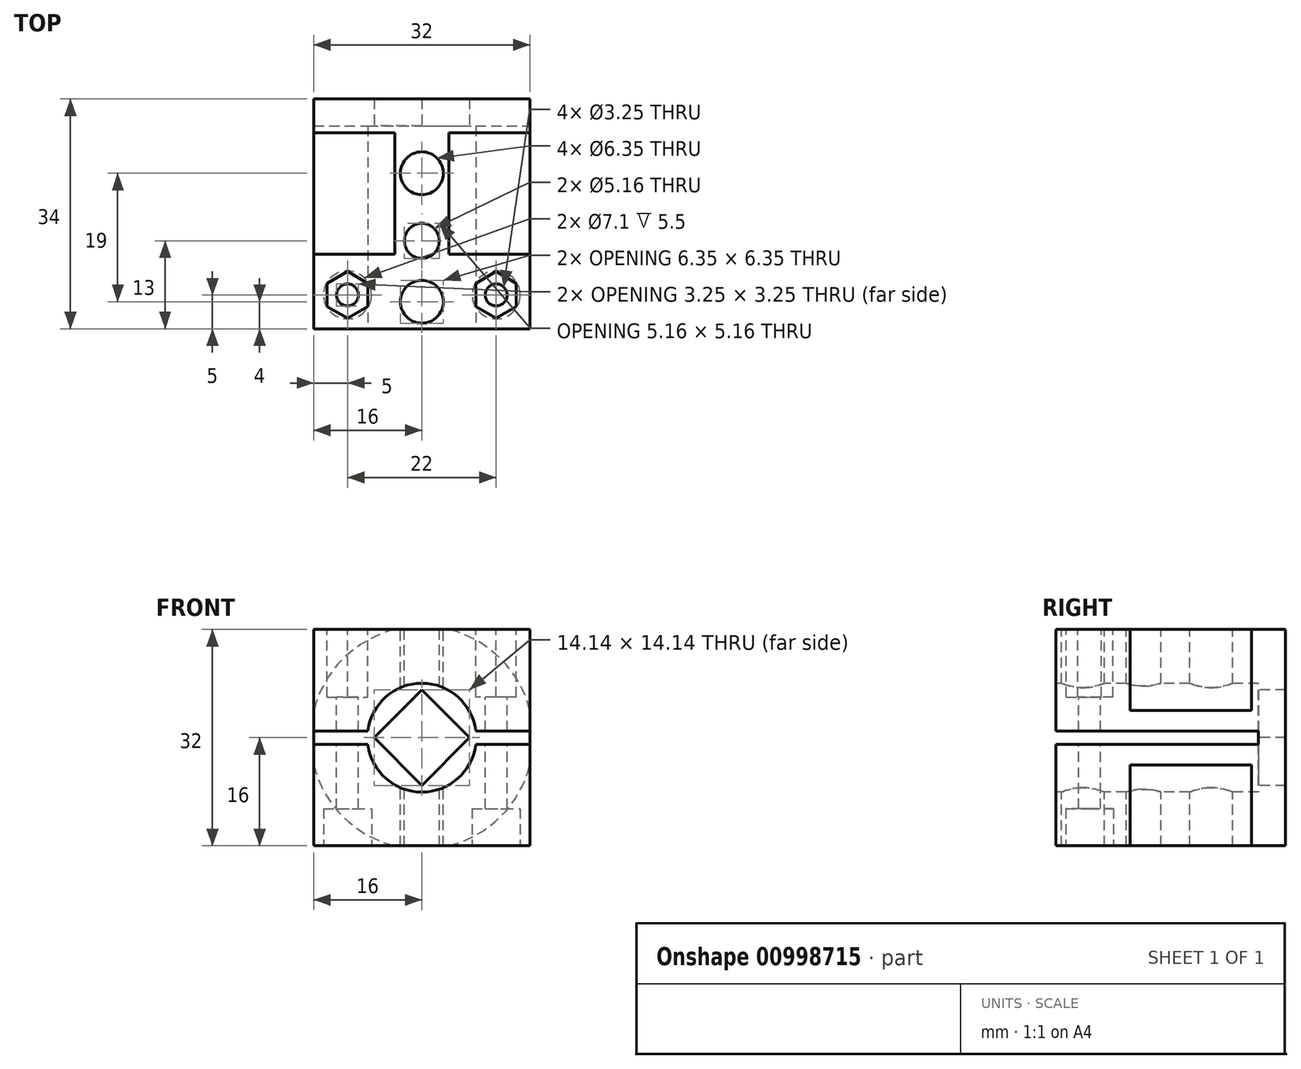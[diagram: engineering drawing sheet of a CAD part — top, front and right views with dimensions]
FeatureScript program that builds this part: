
annotation { "Feature Type Name" : "Feature", "Feature Type Description" : "" }
export const myFeature = defineFeature(function(context is Context, id is Id, definition is map)
    precondition{}
    {
        {
            var Q0;
            Q0=qCreatedBy(makeId("Front.planeOp"),FACE);
            var sketch = newSketch(context, id + "F0", { "sketchPlane" : qUnion([Q0])});
            skLineSegment(sketch, "E0.bottom", {"start": v(16, -16) * mm, "end": v(-16, -16) * mm});
            skLineSegment(sketch, "E0.top", {"start": v(16, 16) * mm, "end": v(-16, 16) * mm});
            skLineSegment(sketch, "E0.left", {"start": v(16, -16) * mm, "end": v(16, 16) * mm});
            skLineSegment(sketch, "E0.right", {"start": v(-16, -16) * mm, "end": v(-16, 16) * mm});
            skPoint(sketch, "E0.middle", {"position": v(0, 0) * mm});
            skSolve(sketch);
        }
        {
            var Q0;
            Q0 = qSketchRegion(id + "F0", true);
            extrude(context, id + "F1", {"entities" : qUnion([Q0]), "endBound" : BoundingType.SYMMETRIC, "depth" : 34 * mm, "offsetDistance" : 25 * mm});
        }
        {
            var Q0;
            Q0=qCreatedBy(makeId("Front.planeOp"),FACE);
            var sketch = newSketch(context, id + "F2", { "sketchPlane" : qUnion([Q0])});
            skCircle(sketch, "E1", {"center": v(0, 0) * mm, "radius": 8.05 * mm});
            skSolve(sketch);
        }
        {
            var Q0;
            Q0 = qSketchRegion(id + "F2", true);
            extrude(context, id + "F3", {"entities" : qUnion([Q0]), "operationType" : NewBodyOperationType.REMOVE, "oppositeDirection" : true, "depth" : 13 * mm, "offsetDistance" : 25 * mm, "hasSecondDirection" : true, "secondDirectionOppositeDirection" : false, "secondDirectionDepth" : 17 * mm});
        }
        {
            var Q0;
            Q0=qCreatedBy(makeId("Right.planeOp"),FACE);
            var sketch = newSketch(context, id + "F4", { "sketchPlane" : qUnion([Q0])});
            skLineSegment(sketch, "E2", {"start": v(-19, 1) * mm, "end": v(13, 1) * mm});
            skLineSegment(sketch, "E3", {"start": v(13, 1) * mm, "end": v(13, -1) * mm});
            skLineSegment(sketch, "E4", {"start": v(13, -1) * mm, "end": v(-19, -1) * mm});
            skLineSegment(sketch, "E5", {"start": v(-19, -1) * mm, "end": v(-19, 1) * mm});
            skSolve(sketch);
        }
        {
            var Q0;
            Q0=makeQuery(id+"F4.imprint","IMPRINT",FACE,{"disambiguationData":[TD([[makeQuery(id+"F4.imprint","IMPRINT",EDGE,{"derivedFrom":sQuery(id+"F4.wireOp",EDGE,"E2")}),-1.0]])]});
            extrude(context, id + "F5", {"entities" : qUnion([Q0]), "operationType" : NewBodyOperationType.REMOVE, "endBound" : BoundingType.THROUGH_ALL, "oppositeDirection" : true, "depth" : 25 * mm, "offsetDistance" : 25 * mm, "hasSecondDirection" : true, "secondDirectionBound" : SecondDirectionBoundingType.THROUGH_ALL, "secondDirectionOppositeDirection" : false, "secondDirectionDepth" : 25 * mm});
        }
        {
            var Q0;
            Q0=qCreatedBy(makeId("Top.planeOp"),FACE);
            var sketch = newSketch(context, id + "F6", { "sketchPlane" : qUnion([Q0])});
            skLineSegment(sketch, "E6", {"start": v(0, -53.15) * mm, "end": v(0, 37.76) * mm, "construction": true});
            skCircle(sketch, "E7", {"center": v(0, 6) * mm, "radius": 3.18 * mm});
            skCircle(sketch, "E8", {"center": v(0, -4) * mm, "radius": 2.58 * mm});
            skCircle(sketch, "E9", {"center": v(0, -13) * mm, "radius": 3.18 * mm});
            skLineSegment(sketch, "E10.0.0", {"start": v(7.99, 13) * mm, "end": v(-7.99, 13) * mm, "construction": true});
            skSolve(sketch);
        }
        {
            var Q0;
            Q0 = qSketchRegion(id + "F6", true);
            extrude(context, id + "F7", {"entities" : qUnion([Q0]), "operationType" : NewBodyOperationType.REMOVE, "endBound" : BoundingType.THROUGH_ALL, "oppositeDirection" : true, "depth" : 25 * mm, "offsetDistance" : 25 * mm, "hasSecondDirection" : true, "secondDirectionBound" : SecondDirectionBoundingType.THROUGH_ALL, "secondDirectionOppositeDirection" : false, "secondDirectionDepth" : 25 * mm});
        }
        {
            var Q0;
            Q0=makeQuery(id+"F1.opExtrude","SWEPT_FACE",FACE,{"disambiguationData":[OSD([sQuery(id+"F0.wireOp",EDGE,"E0.top")])]});
            var sketch = newSketch(context, id + "F8", { "sketchPlane" : qUnion([Q0])});
            skLineSegment(sketch, "E11.0", {"start": v(16, -17) * mm, "end": v(-16, -17) * mm, "construction": true});
            skLineSegment(sketch, "E12.1", {"start": v(16, -17) * mm, "end": v(16, 17) * mm, "construction": true});
            skLineSegment(sketch, "E13.0", {"start": v(16, 17) * mm, "end": v(-16, 17) * mm, "construction": true});
            skLineSegment(sketch, "E14.0", {"start": v(-16, -17) * mm, "end": v(-16, 17) * mm, "construction": true});
            skCircle(sketch, "E15", {"center": v(-11, -12) * mm, "radius": 1.63 * mm});
            skCircle(sketch, "E16", {"center": v(11, -12) * mm, "radius": 1.63 * mm});
            skSolve(sketch);
        }
        {
            var Q0;
            Q0 = qSketchRegion(id + "F8", true);
            extrude(context, id + "F9", {"entities" : qUnion([Q0]), "operationType" : NewBodyOperationType.REMOVE, "endBound" : BoundingType.THROUGH_ALL, "oppositeDirection" : true, "depth" : 25 * mm, "offsetDistance" : 25 * mm});
        }
        {
            var Q0;
            Q0=makeQuery(id+"F1.opExtrude","SWEPT_FACE",FACE,{"disambiguationData":[OSD([sQuery(id+"F0.wireOp",EDGE,"E0.bottom")])]});
            var sketch = newSketch(context, id + "F10", { "sketchPlane" : qUnion([Q0])});
            skCircle(sketch, "E17", {"center": v(11, 12) * mm, "radius": 3.55 * mm});
            skCircle(sketch, "E18", {"center": v(-11, 12) * mm, "radius": 3.55 * mm});
            skSolve(sketch);
        }
        {
            var Q0;
            Q0=makeQuery(id+"F1.opExtrude","SWEPT_FACE",FACE,{"disambiguationData":[OSD([sQuery(id+"F0.wireOp",EDGE,"E0.top")])]});
            var sketch = newSketch(context, id + "F11", { "sketchPlane" : qUnion([Q0])});
            skCircle(sketch, "E19.cCircle", {"center": v(-11, -12) * mm, "radius": 3 * mm, "construction": true});
            skLineSegment(sketch, "E19.0", {"start": v(-8, -10.27) * mm, "end": v(-8, -13.73) * mm});
            skLineSegment(sketch, "E19.1", {"start": v(-8, -13.73) * mm, "end": v(-11, -15.46) * mm});
            skLineSegment(sketch, "E19.2", {"start": v(-11, -15.46) * mm, "end": v(-14, -13.73) * mm});
            skLineSegment(sketch, "E19.3", {"start": v(-14, -13.73) * mm, "end": v(-14, -10.27) * mm});
            skLineSegment(sketch, "E19.4", {"start": v(-14, -10.27) * mm, "end": v(-11, -8.54) * mm});
            skLineSegment(sketch, "E19.5", {"start": v(-11, -8.54) * mm, "end": v(-8, -10.27) * mm});
            skPoint(sketch, "E19.0.midPoint", {"position": v(-8, -12) * mm});
            skCircle(sketch, "E20.cCircle", {"center": v(11, -12) * mm, "radius": 3 * mm, "construction": true});
            skLineSegment(sketch, "E20.0", {"start": v(8, -13.73) * mm, "end": v(8, -10.27) * mm});
            skLineSegment(sketch, "E20.1", {"start": v(8, -10.27) * mm, "end": v(11, -8.54) * mm});
            skLineSegment(sketch, "E20.2", {"start": v(11, -8.54) * mm, "end": v(14, -10.27) * mm});
            skLineSegment(sketch, "E20.3", {"start": v(14, -10.27) * mm, "end": v(14, -13.73) * mm});
            skLineSegment(sketch, "E20.4", {"start": v(14, -13.73) * mm, "end": v(11, -15.46) * mm});
            skLineSegment(sketch, "E20.5", {"start": v(11, -15.46) * mm, "end": v(8, -13.73) * mm});
            skPoint(sketch, "E20.0.midPoint", {"position": v(8, -12) * mm});
            skSolve(sketch);
        }
        {
            var Q0;
            Q0 = qSketchRegion(id + "F10", true);
            extrude(context, id + "F12", {"entities" : qUnion([Q0]), "operationType" : NewBodyOperationType.REMOVE, "oppositeDirection" : true, "depth" : 5.5 * mm, "offsetDistance" : 25 * mm});
        }
        {
            var Q0;
            Q0 = qSketchRegion(id + "F11", true);
            extrude(context, id + "F13", {"entities" : qUnion([Q0]), "operationType" : NewBodyOperationType.REMOVE, "oppositeDirection" : true, "depth" : 10 * mm, "offsetDistance" : 25 * mm});
        }
        {
            var Q0;
            Q0=makeQuery(id+"F5.boolean.opBoolean","MERGE",FACE,{"derivedFrom":[makeQuery(id+"F3.boolean.opBoolean","COPY",FACE,{"derivedFrom":makeQuery(id+"F3.opExtrude","CAP_FACE",FACE,{"disambiguationData":[OSD([sQuery(id+"F2.wireOp",EDGE,"E1")])],"isStart":false})})],"fromTools":[makeQuery(id+"F5.opExtrude","SWEPT_FACE",FACE,{"disambiguationData":[OSD([sQuery(id+"F4.wireOp",EDGE,"E3")])]})]});
            var sketch = newSketch(context, id + "F14", { "sketchPlane" : qUnion([Q0])});
            skCircle(sketch, "E21.cCircle", {"center": v(0, 0) * mm, "radius": 5 * mm, "construction": true});
            skLineSegment(sketch, "E21.0", {"start": v(7.07, 0) * mm, "end": v(0, -7.07) * mm});
            skLineSegment(sketch, "E21.1", {"start": v(0, -7.07) * mm, "end": v(-7.07, 0) * mm});
            skLineSegment(sketch, "E21.2", {"start": v(-7.07, 0) * mm, "end": v(0, 7.07) * mm});
            skLineSegment(sketch, "E21.3", {"start": v(0, 7.07) * mm, "end": v(7.07, 0) * mm});
            skPoint(sketch, "E21.0.midPoint", {"position": v(3.54, -3.54) * mm});
            skLineSegment(sketch, "E22", {"start": v(0, 0) * mm, "end": v(-7.12, 0) * mm, "construction": true});
            skSolve(sketch);
        }
        {
            var Q0;
            Q0=makeQuery(id+"F14.imprint","IMPRINT",FACE,{"disambiguationData":[TD([[makeQuery(id+"F14.imprint","IMPRINT",EDGE,{"derivedFrom":sQuery(id+"F14.wireOp",EDGE,"E21.0")}),-1.0]])]});
            extrude(context, id + "F15", {"entities" : qUnion([Q0]), "operationType" : NewBodyOperationType.REMOVE, "endBound" : BoundingType.THROUGH_ALL, "oppositeDirection" : true, "depth" : 25 * mm, "offsetDistance" : 25 * mm});
        }
        {
            var Q0;
            Q0=qCreatedBy(makeId("Top.planeOp"),FACE);
            var sketch = newSketch(context, id + "F16", { "sketchPlane" : qUnion([Q0])});
            skLineSegment(sketch, "E23.0.0", {"start": v(16, 17) * mm, "end": v(-16, 17) * mm, "construction": true});
            skLineSegment(sketch, "E23.0.1", {"start": v(-16, 17) * mm, "end": v(-16, -17) * mm, "construction": true});
            skLineSegment(sketch, "E23.0.2", {"start": v(-16, -17) * mm, "end": v(16, -17) * mm, "construction": true});
            skLineSegment(sketch, "E23.0.3", {"start": v(16, -17) * mm, "end": v(16, 17) * mm, "construction": true});
            skLineSegment(sketch, "E24.bottom", {"start": v(16.5, -6) * mm, "end": v(26, -6) * mm});
            skLineSegment(sketch, "E24.top", {"start": v(16.5, 12) * mm, "end": v(26, 12) * mm});
            skLineSegment(sketch, "E24.left", {"start": v(16.5, -6) * mm, "end": v(16.5, 12) * mm});
            skLineSegment(sketch, "E24.right", {"start": v(26, -6) * mm, "end": v(26, 12) * mm});
            skLineSegment(sketch, "E25", {"start": v(0, 14.72) * mm, "end": v(0, -21.59) * mm, "construction": true});
            skSolve(sketch);
        }
        {
            var Q0;
            Q0 = qSketchRegion(id + "F16", true);
            var Q1;
            Q1=sQuery(id+"F16.wireOp",EDGE,"E25");
            revolve(context, id + "F17", {"operationType" : NewBodyOperationType.REMOVE, "surfaceOperationType" : NewSurfaceOperationType.NEW, "entities" : qUnion([Q0]), "axis" : qUnion([Q1]), "revolveType" : RevolveType.FULL, "oppositeDirection" : true});
        }
    });
